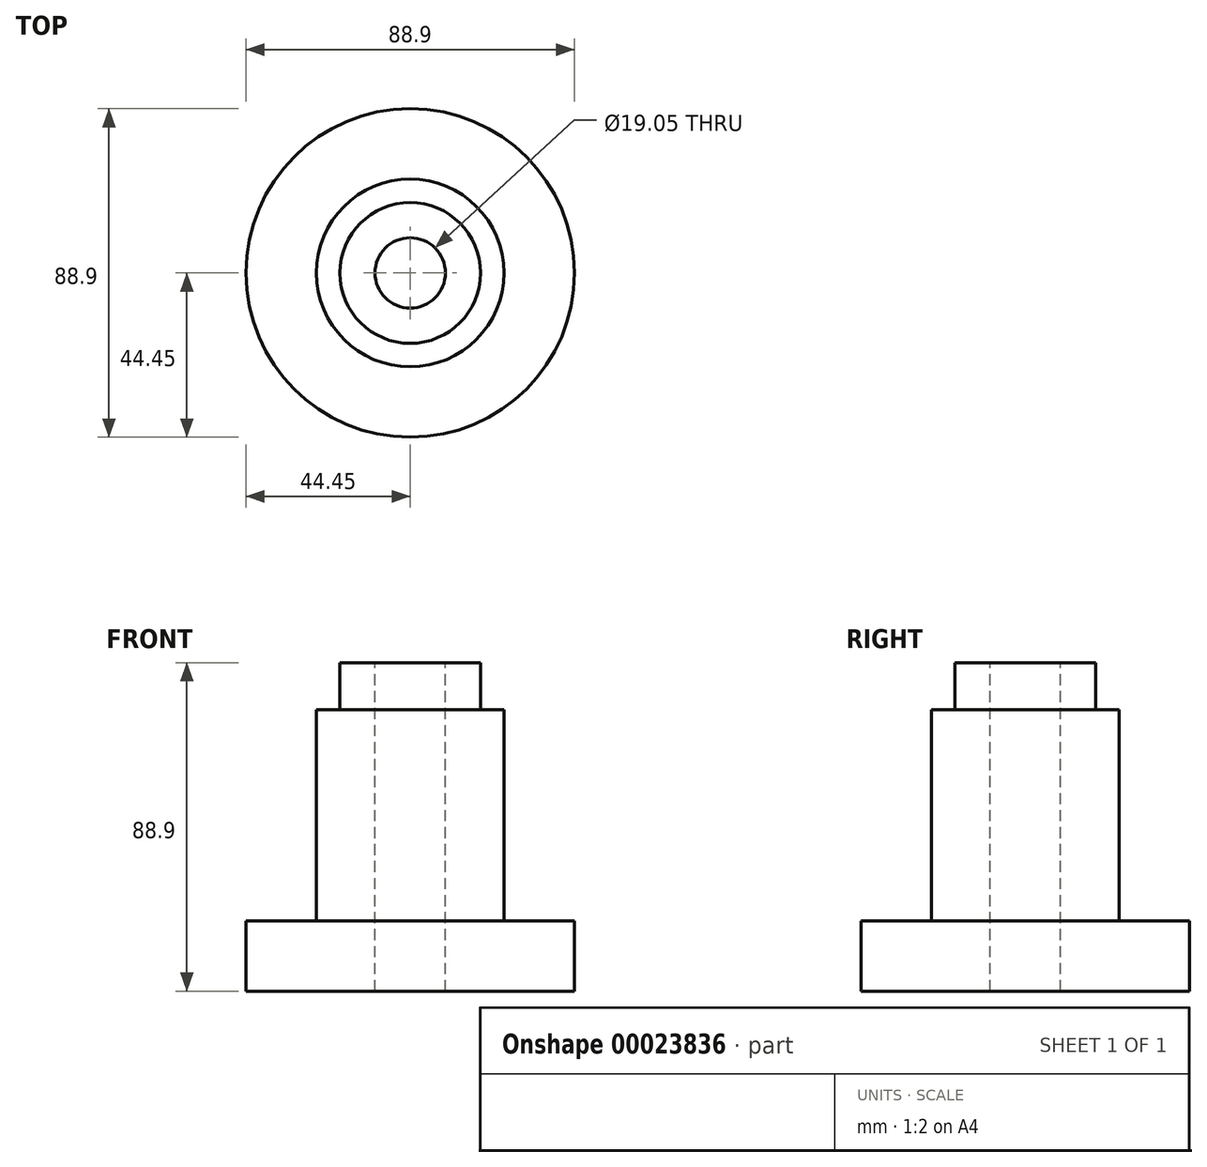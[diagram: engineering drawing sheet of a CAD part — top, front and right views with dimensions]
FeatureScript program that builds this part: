
annotation { "Feature Type Name" : "Feature", "Feature Type Description" : "" }
export const myFeature = defineFeature(function(context is Context, id is Id, definition is map)
    precondition{}
    {
        {
            var Q0;
            Q0=qCreatedBy(makeId("Front.planeOp"),FACE);
            var sketch = newSketch(context, id + "F0", { "sketchPlane" : qUnion([Q0])});
            skLineSegment(sketch, "E0.bottom", {"start": v(-9.52, -8.34) * mm, "end": v(-44.45, -8.34) * mm});
            skLineSegment(sketch, "E0.top", {"start": v(-9.52, -27.4) * mm, "end": v(-44.45, -27.4) * mm});
            skLineSegment(sketch, "E0.left", {"start": v(-9.52, -8.34) * mm, "end": v(-9.52, -27.4) * mm});
            skLineSegment(sketch, "E0.right", {"start": v(-44.45, -8.34) * mm, "end": v(-44.45, -27.4) * mm});
            skLineSegment(sketch, "E1", {"start": v(0, 77.38) * mm, "end": v(0, -78.96) * mm, "construction": true});
            skLineSegment(sketch, "E2.bottom", {"start": v(-9.52, -8.34) * mm, "end": v(-25.4, -8.34) * mm});
            skLineSegment(sketch, "E2.top", {"start": v(-9.53, 48.8) * mm, "end": v(-25.4, 48.8) * mm});
            skLineSegment(sketch, "E2.left", {"start": v(-9.52, -8.34) * mm, "end": v(-9.53, 48.8) * mm});
            skLineSegment(sketch, "E2.right", {"start": v(-25.4, -8.34) * mm, "end": v(-25.4, 48.8) * mm});
            skLineSegment(sketch, "E3.bottom", {"start": v(-9.53, 48.8) * mm, "end": v(-19.05, 48.8) * mm});
            skLineSegment(sketch, "E3.top", {"start": v(-9.53, 61.5) * mm, "end": v(-19.05, 61.5) * mm});
            skLineSegment(sketch, "E3.left", {"start": v(-9.53, 48.8) * mm, "end": v(-9.53, 61.5) * mm});
            skLineSegment(sketch, "E3.right", {"start": v(-19.05, 48.8) * mm, "end": v(-19.05, 61.5) * mm});
            skSolve(sketch);
        }
        {
            var Q0;
            Q0 = qSketchRegion(id + "F0", true);
            var Q1;
            Q1=sQuery(id+"F0.wireOp",EDGE,"E1");
            revolve(context, id + "F1", {"entities" : qUnion([Q0]), "axis" : qUnion([Q1]), "revolveType" : RevolveType.FULL});
        }
    });
